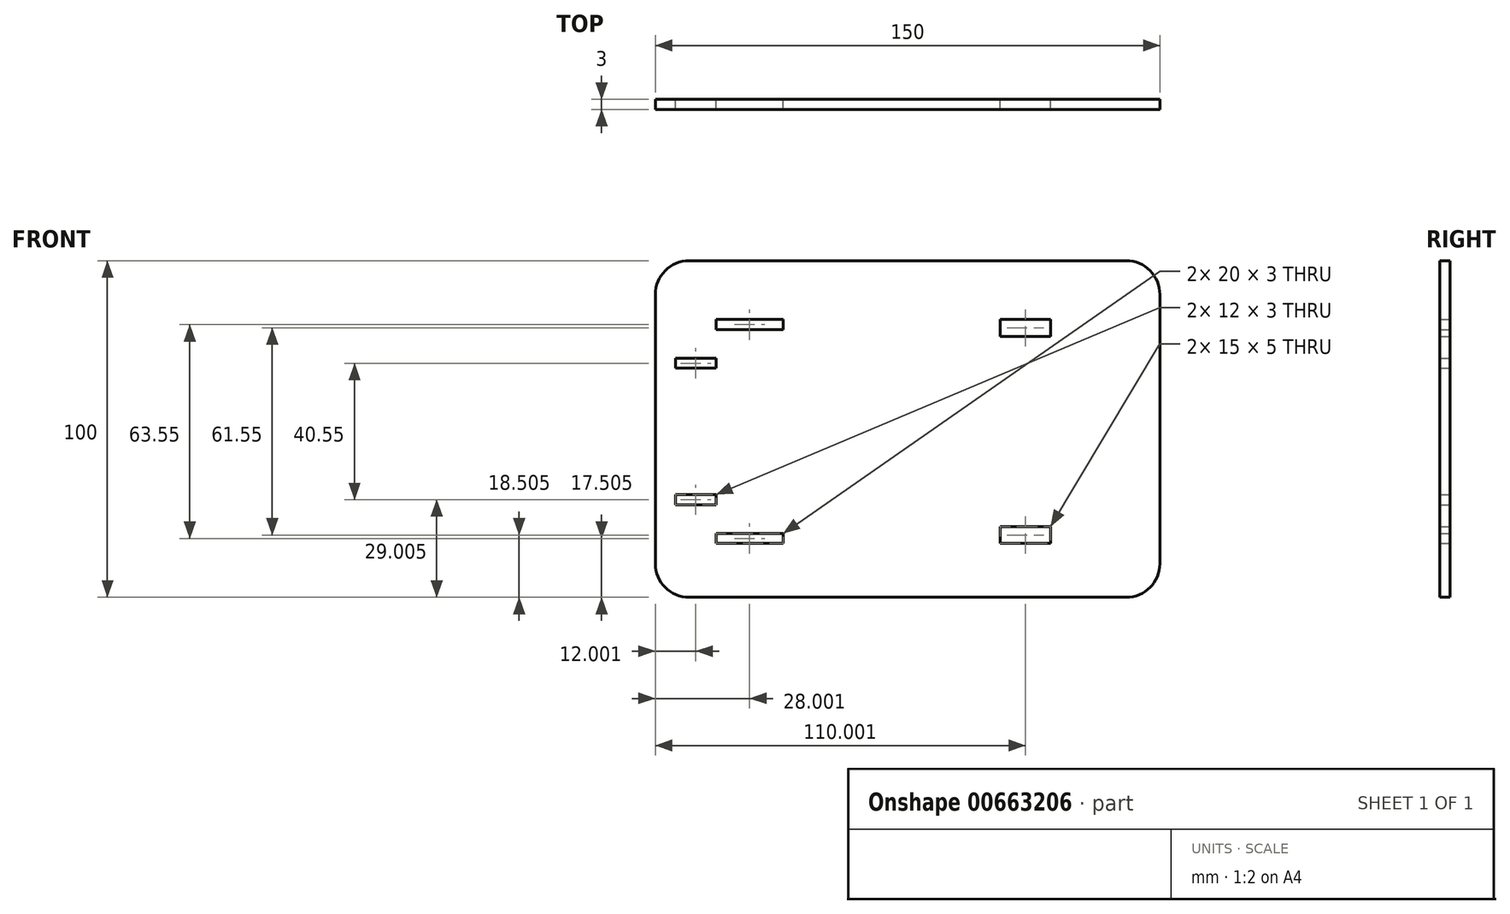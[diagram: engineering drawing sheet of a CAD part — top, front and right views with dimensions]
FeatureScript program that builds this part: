
annotation { "Feature Type Name" : "Feature", "Feature Type Description" : "" }
export const myFeature = defineFeature(function(context is Context, id is Id, definition is map)
    precondition{}
    {
        {
            var Q0;
            Q0=qCreatedBy(makeId("Front.planeOp"),FACE);
            var sketch = newSketch(context, id + "F0", { "sketchPlane" : qUnion([Q0])});
            skLineSegment(sketch, "E0", {"start": v(-75.28, 40.72) * mm, "end": v(-75.28, -39.28) * mm});
            skLineSegment(sketch, "E1", {"start": v(-65.28, -49.28) * mm, "end": v(64.72, -49.28) * mm});
            skLineSegment(sketch, "E2", {"start": v(74.72, -39.28) * mm, "end": v(74.72, 40.72) * mm});
            skLineSegment(sketch, "E3", {"start": v(64.72, 50.72) * mm, "end": v(-65.28, 50.72) * mm});
            skPoint(sketch, "E4.visualSharp", {"position": v(-75.28, 50.72) * mm});
            skArc(sketch, "E4.filletArc", {"start": v(-65.28, 50.72) * mm, "mid": v(-72.35, 47.8) * mm, "end": v(-75.28, 40.72) * mm});
            skPoint(sketch, "E5.visualSharp", {"position": v(-75.28, -49.28) * mm});
            skArc(sketch, "E5.filletArc", {"start": v(-75.28, -39.28) * mm, "mid": v(-72.35, -46.35) * mm, "end": v(-65.28, -49.28) * mm});
            skPoint(sketch, "E6.visualSharp", {"position": v(74.72, -49.28) * mm});
            skArc(sketch, "E6.filletArc", {"start": v(64.72, -49.28) * mm, "mid": v(71.8, -46.35) * mm, "end": v(74.72, -39.28) * mm});
            skPoint(sketch, "E7.visualSharp", {"position": v(74.72, 50.72) * mm});
            skArc(sketch, "E7.filletArc", {"start": v(74.72, 40.72) * mm, "mid": v(71.8, 47.8) * mm, "end": v(64.72, 50.72) * mm});
            skLineSegment(sketch, "E8.bottom", {"start": v(27.22, -28.28) * mm, "end": v(42.22, -28.28) * mm});
            skLineSegment(sketch, "E8.top", {"start": v(27.22, -33.28) * mm, "end": v(42.22, -33.28) * mm});
            skLineSegment(sketch, "E8.left", {"start": v(27.22, -28.28) * mm, "end": v(27.22, -33.28) * mm});
            skLineSegment(sketch, "E8.right", {"start": v(42.22, -28.28) * mm, "end": v(42.22, -33.28) * mm});
            skLineSegment(sketch, "E9.bottom", {"start": v(-69.28, -18.78) * mm, "end": v(-57.28, -18.78) * mm});
            skLineSegment(sketch, "E9.top", {"start": v(-69.28, -21.78) * mm, "end": v(-57.28, -21.78) * mm});
            skLineSegment(sketch, "E9.left", {"start": v(-69.28, -18.78) * mm, "end": v(-69.28, -21.78) * mm});
            skLineSegment(sketch, "E9.right", {"start": v(-57.28, -18.78) * mm, "end": v(-57.28, -21.78) * mm});
            skLineSegment(sketch, "E10.bottom", {"start": v(-57.28, -30.28) * mm, "end": v(-37.28, -30.28) * mm});
            skLineSegment(sketch, "E10.top", {"start": v(-57.28, -33.28) * mm, "end": v(-37.28, -33.28) * mm});
            skLineSegment(sketch, "E10.left", {"start": v(-57.28, -30.28) * mm, "end": v(-57.28, -33.28) * mm});
            skLineSegment(sketch, "E10.right", {"start": v(-37.28, -30.28) * mm, "end": v(-37.28, -33.28) * mm});
            skLineSegment(sketch, "E11.MirrorCS", {"start": v(-37.28, 30.28) * mm, "end": v(-37.28, 33.28) * mm});
            skLineSegment(sketch, "E12.MirrorCS", {"start": v(-57.28, 18.78) * mm, "end": v(-57.28, 21.78) * mm});
            skLineSegment(sketch, "E13.MirrorCS", {"start": v(-69.28, 18.78) * mm, "end": v(-69.28, 21.78) * mm});
            skLineSegment(sketch, "E14.MirrorCS", {"start": v(-57.28, 30.28) * mm, "end": v(-57.28, 33.28) * mm});
            skLineSegment(sketch, "E15.MirrorCS", {"start": v(27.22, 28.28) * mm, "end": v(27.22, 33.28) * mm});
            skLineSegment(sketch, "E16.MirrorCS", {"start": v(42.22, 28.28) * mm, "end": v(42.22, 33.28) * mm});
            skLineSegment(sketch, "E17.MirrorCS", {"start": v(-69.28, 21.78) * mm, "end": v(-57.28, 21.78) * mm});
            skLineSegment(sketch, "E18.MirrorCS", {"start": v(27.22, 28.28) * mm, "end": v(42.22, 28.28) * mm});
            skLineSegment(sketch, "E19.MirrorCS", {"start": v(-57.28, 33.28) * mm, "end": v(-37.28, 33.28) * mm});
            skLineSegment(sketch, "E20.MirrorCS", {"start": v(-57.28, 30.28) * mm, "end": v(-37.28, 30.28) * mm});
            skLineSegment(sketch, "E21.MirrorCS", {"start": v(27.22, 33.28) * mm, "end": v(42.22, 33.28) * mm});
            skLineSegment(sketch, "E22.MirrorCS", {"start": v(-69.28, 18.78) * mm, "end": v(-57.28, 18.78) * mm});
            skSolve(sketch);
        }
        {
            var Q0;
            Q0 = qSketchRegion(id + "F0", true);
            extrude(context, id + "F1", {"entities" : qUnion([Q0]), "depth" : 3 * mm, "offsetDistance" : 25 * mm});
        }
    });
